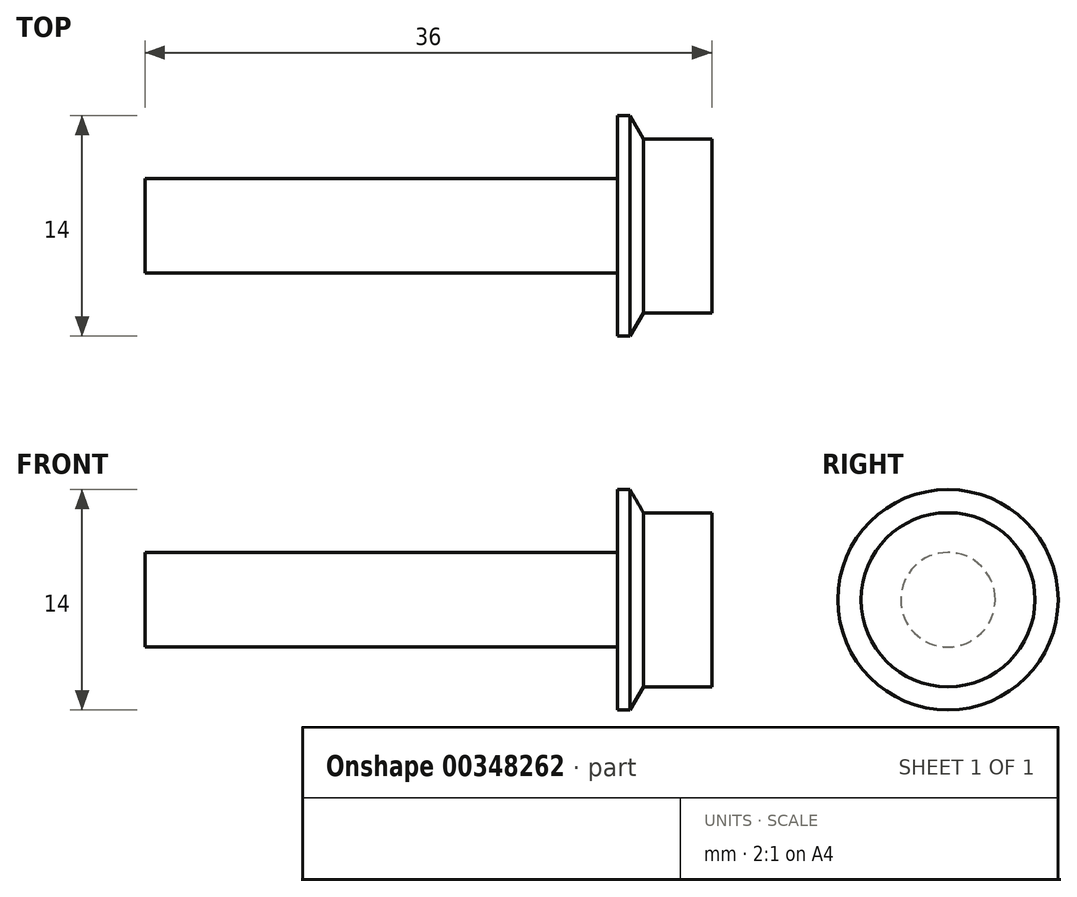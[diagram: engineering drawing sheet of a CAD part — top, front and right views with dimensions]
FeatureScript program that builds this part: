
annotation { "Feature Type Name" : "Feature", "Feature Type Description" : "" }
export const myFeature = defineFeature(function(context is Context, id is Id, definition is map)
    precondition{}
    {
        {
            var Q0;
            Q0=qCreatedBy(makeId("Top.planeOp"),FACE);
            var sketch = newSketch(context, id + "F0", { "sketchPlane" : qUnion([Q0])});
            skLineSegment(sketch, "E0", {"start": v(0, 7) * mm, "end": v(0.8, 7) * mm});
            skLineSegment(sketch, "E1", {"start": v(1.65, 5.53) * mm, "end": v(6, 5.53) * mm});
            skLineSegment(sketch, "E2", {"start": v(6, 5.53) * mm, "end": v(6, 0) * mm});
            skLineSegment(sketch, "E3", {"start": v(6, 0) * mm, "end": v(-30, 0) * mm});
            skLineSegment(sketch, "E4", {"start": v(-30, 0) * mm, "end": v(-30, 3) * mm});
            skLineSegment(sketch, "E5", {"start": v(-30, 3) * mm, "end": v(0, 3) * mm});
            skLineSegment(sketch, "E6", {"start": v(0, 3) * mm, "end": v(0, 7) * mm});
            skLineSegment(sketch, "E7", {"start": v(0.8, 7) * mm, "end": v(1.65, 5.53) * mm});
            skLineSegment(sketch, "E8", {"start": v(-58.77, 0) * mm, "end": v(37.59, 0) * mm, "construction": true});
            skSolve(sketch);
        }
        {
            var Q0;
            Q0=makeQuery(id+"F0.imprint","IMPRINT",FACE,{"disambiguationData":[TD([[makeQuery(id+"F0.imprint","IMPRINT",EDGE,{"derivedFrom":sQuery(id+"F0.wireOp",EDGE,"E0")}),-1.0]])]});
            var Q1;
            Q1=sQuery(id+"F0.wireOp",EDGE,"E8");
            revolve(context, id + "F1", {"entities" : qUnion([Q0]), "axis" : qUnion([Q1]), "revolveType" : RevolveType.FULL});
        }
    });
